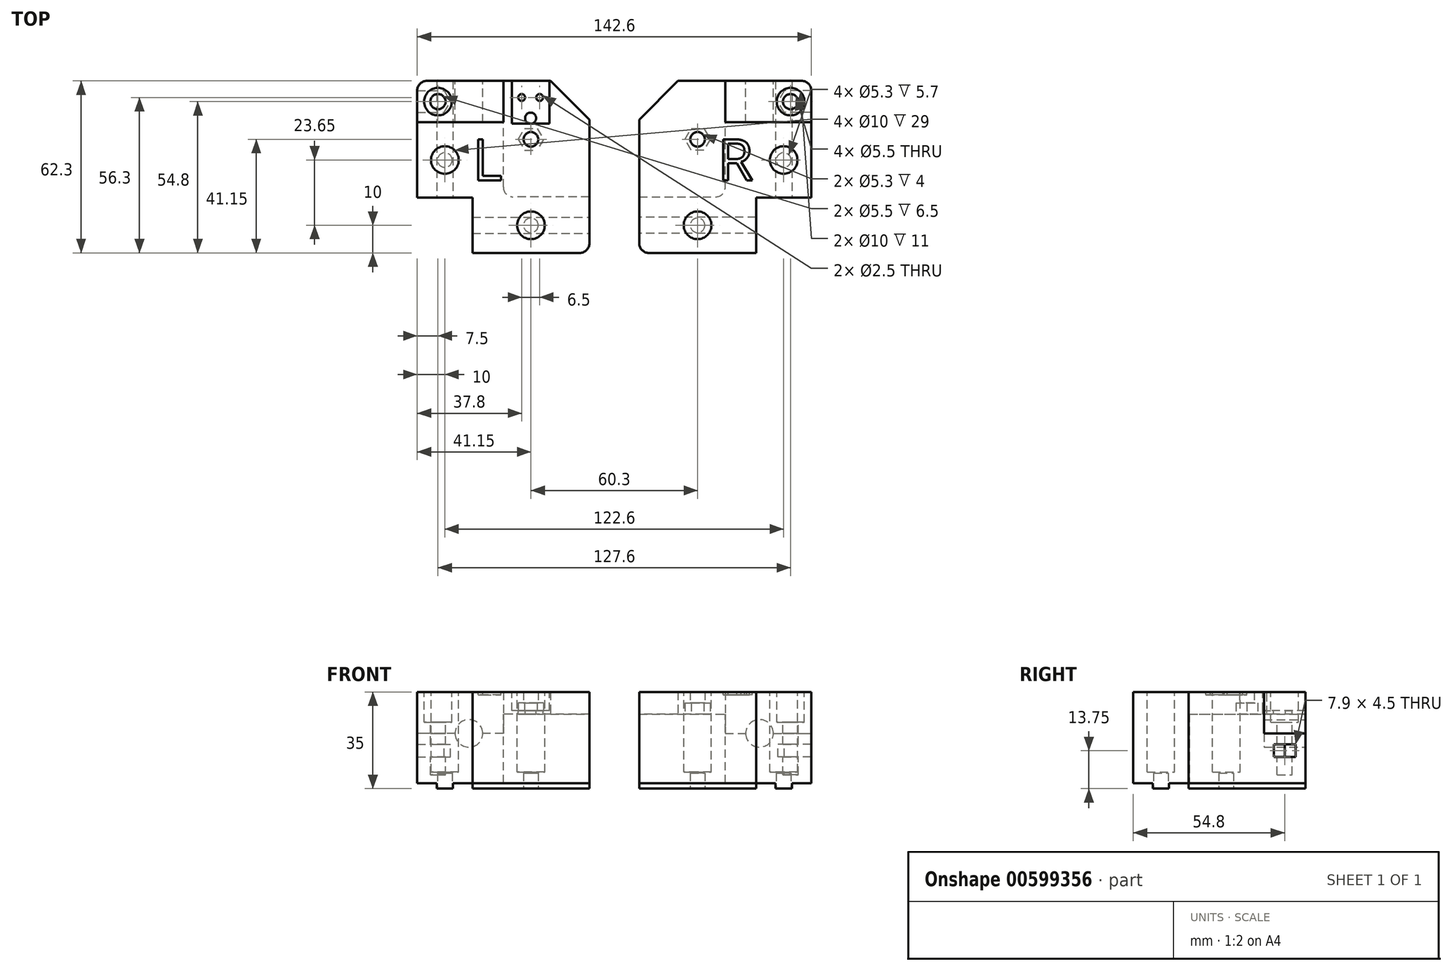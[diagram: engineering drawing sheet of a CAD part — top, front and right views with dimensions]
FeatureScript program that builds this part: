
annotation { "Feature Type Name" : "Feature", "Feature Type Description" : "" }
export const myFeature = defineFeature(function(context is Context, id is Id, definition is map)
    precondition{}
    {
        {
            var Q0;
            Q0=qCreatedBy(makeId("Top.planeOp"),FACE);
            var sketch = newSketch(context, id + "F0", { "sketchPlane" : qUnion([Q0])});
            skLineSegment(sketch, "E0.bottom", {"start": v(-21.15, 35) * mm, "end": v(41.15, 35) * mm});
            skLineSegment(sketch, "E0.top", {"start": v(-21.15, -27.3) * mm, "end": v(21.15, -27.3) * mm});
            skLineSegment(sketch, "E0.left", {"start": v(-21.15, 35) * mm, "end": v(-21.15, -27.3) * mm});
            skLineSegment(sketch, "E0.right", {"start": v(41.15, 35) * mm, "end": v(41.15, -7.3) * mm});
            skLineSegment(sketch, "E1.top", {"start": v(41.15, -7.3) * mm, "end": v(21.15, -7.3) * mm});
            skLineSegment(sketch, "E1.right", {"start": v(21.15, -27.3) * mm, "end": v(21.15, -7.3) * mm});
            skCircle(sketch, "E2", {"center": v(31.15, 13.85) * mm, "radius": 2.65 * mm});
            skPoint(sketch, "E3.centerSnap0", {"position": v(0, -27.3) * mm});
            skCircle(sketch, "E4", {"center": v(0, 13.85) * mm, "radius": 2.65 * mm});
            skPoint(sketch, "E5.centerSnap0", {"position": v(21.15, -17.3) * mm});
            skCircle(sketch, "E6", {"center": v(7.5, -17.3) * mm, "radius": 2.65 * mm});
            skSolve(sketch);
        }
        {
            var Q0;
            Q0=qSketchRegion(id+"F0",true);
            extrude(context, id + "F1", {"entities" : qUnion([Q0]), "depth" : 33 * mm});
        }
        {
            var Q0;
            Q0=makeQuery(id+"F1.opExtrude","CAP_FACE",FACE,{"disambiguationData":[OSD([sQuery(id+"F0.wireOp",EDGE,"E0.bottom"),sQuery(id+"F0.wireOp",EDGE,"E0.top"),sQuery(id+"F0.wireOp",EDGE,"E0.left"),sQuery(id+"F0.wireOp",EDGE,"E0.right"),sQuery(id+"F0.wireOp",EDGE,"E1.top"),sQuery(id+"F0.wireOp",EDGE,"E1.right"),sQuery(id+"F0.wireOp",EDGE,"E2"),sQuery(id+"F0.wireOp",EDGE,"74evYqRE-stiJ-cLZB-LkAt-MwOgdlZv3zJH"),sQuery(id+"F0.wireOp",EDGE,"YSbFCtBf-OZUa-blBg-jqSk-ddDIdjAn90QF"),sQuery(id+"F0.wireOp",EDGE,"E3"),sQuery(id+"F0.wireOp",EDGE,"E4")])],"isStart":true});
            var sketch = newSketch(context, id + "F2", { "sketchPlane" : qUnion([Q0])});
            skCircle(sketch, "E7.0", {"center": v(0, -13.85) * mm, "radius": 2.65 * mm, "construction": true});
            skCircle(sketch, "E8", {"center": v(0, -13.85) * mm, "radius": 3.95 * mm, "construction": true});
            skLineSegment(sketch, "E9", {"start": v(0, -20.58) * mm, "end": v(0, -4.16) * mm, "construction": true});
            skLineSegment(sketch, "E10", {"start": v(-6.74, -13.85) * mm, "end": v(6.1, -13.85) * mm, "construction": true});
            skLineSegment(sketch, "E11", {"start": v(-3.95, -16.13) * mm, "end": v(-3.95, -11.57) * mm});
            skLineSegment(sketch, "E12", {"start": v(-3.95, -11.57) * mm, "end": v(0, -9.29) * mm});
            skLineSegment(sketch, "E13", {"start": v(3.95, -16.13) * mm, "end": v(0, -18.41) * mm});
            skLineSegment(sketch, "E14", {"start": v(0, -18.41) * mm, "end": v(-3.95, -16.13) * mm});
            skLineSegment(sketch, "E15", {"start": v(3.95, -16.13) * mm, "end": v(3.95, -11.57) * mm});
            skLineSegment(sketch, "E16", {"start": v(3.95, -11.57) * mm, "end": v(0, -9.29) * mm});
            skSolve(sketch);
        }
        {
            var Q0;
            Q0=qSketchRegion(id+"F2",true);
            extrude(context, id + "F3", {"entities" : qUnion([Q0]), "operationType" : NewBodyOperationType.REMOVE, "oppositeDirection" : true, "depth" : 29 * mm});
        }
        {
            var Q0;
            Q0=makeQuery(id+"F1.opExtrude","CAP_FACE",FACE,{"disambiguationData":[OSD([sQuery(id+"F0.wireOp",EDGE,"E0.bottom"),sQuery(id+"F0.wireOp",EDGE,"E0.top"),sQuery(id+"F0.wireOp",EDGE,"E0.left"),sQuery(id+"F0.wireOp",EDGE,"E0.right"),sQuery(id+"F0.wireOp",EDGE,"E1.top"),sQuery(id+"F0.wireOp",EDGE,"E1.right"),sQuery(id+"F0.wireOp",EDGE,"E2"),sQuery(id+"F0.wireOp",EDGE,"74evYqRE-stiJ-cLZB-LkAt-MwOgdlZv3zJH"),sQuery(id+"F0.wireOp",EDGE,"YSbFCtBf-OZUa-blBg-jqSk-ddDIdjAn90QF"),sQuery(id+"F0.wireOp",EDGE,"E3"),sQuery(id+"F0.wireOp",EDGE,"E4")])],"isStart":false});
            var sketch = newSketch(context, id + "F4", { "sketchPlane" : qUnion([Q0])});
            skCircle(sketch, "E17.0", {"center": v(31.15, 13.85) * mm, "radius": 2.65 * mm, "construction": true});
            skCircle(sketch, "E18", {"center": v(31.15, 13.85) * mm, "radius": 5 * mm});
            skPoint(sketch, "E19", {"position": v(7.5, -17.3) * mm});
            skCircle(sketch, "E20", {"center": v(7.5, -17.3) * mm, "radius": 5 * mm});
            skSolve(sketch);
        }
        {
            var Q0;
            Q0=qSketchRegion(id+"F4",true);
            extrude(context, id + "F5", {"entities" : qUnion([Q0]), "operationType" : NewBodyOperationType.REMOVE, "oppositeDirection" : true, "depth" : 29 * mm});
        }
        {
            var Q0;
            Q0=makeQuery(id+"F1.opExtrude","CAP_FACE",FACE,{"disambiguationData":[OSD([sQuery(id+"F0.wireOp",EDGE,"E0.bottom"),sQuery(id+"F0.wireOp",EDGE,"E0.top"),sQuery(id+"F0.wireOp",EDGE,"E0.left"),sQuery(id+"F0.wireOp",EDGE,"E0.right"),sQuery(id+"F0.wireOp",EDGE,"E1.top"),sQuery(id+"F0.wireOp",EDGE,"E1.right"),sQuery(id+"F0.wireOp",EDGE,"E2"),sQuery(id+"F0.wireOp",EDGE,"74evYqRE-stiJ-cLZB-LkAt-MwOgdlZv3zJH"),sQuery(id+"F0.wireOp",EDGE,"YSbFCtBf-OZUa-blBg-jqSk-ddDIdjAn90QF"),sQuery(id+"F0.wireOp",EDGE,"E3"),sQuery(id+"F0.wireOp",EDGE,"E4")])],"isStart":true});
            var sketch = newSketch(context, id + "F6", { "sketchPlane" : qUnion([Q0])});
            skLineSegment(sketch, "E21.bottom", {"start": v(28.2, 7.3) * mm, "end": v(34.1, 7.3) * mm});
            skLineSegment(sketch, "E21.top", {"start": v(28.2, -35) * mm, "end": v(34.1, -35) * mm});
            skLineSegment(sketch, "E21.left", {"start": v(28.2, 7.3) * mm, "end": v(28.2, -13.57) * mm});
            skLineSegment(sketch, "E21.right", {"start": v(34.1, 7.3) * mm, "end": v(34.1, -13.57) * mm});
            skCircle(sketch, "E22.0", {"center": v(31.15, -13.85) * mm, "radius": 2.65 * mm});
            skLineSegment(sketch, "E23.trimOffspring", {"start": v(28.2, -13.57) * mm, "end": v(28.2, -35) * mm});
            skLineSegment(sketch, "E24.trimOffspring", {"start": v(34.1, -13.57) * mm, "end": v(34.1, -35) * mm});
            skLineSegment(sketch, "E25.bottom", {"start": v(-21.15, 20.25) * mm, "end": v(21.15, 20.25) * mm});
            skLineSegment(sketch, "E25.top", {"start": v(-21.15, 14.35) * mm, "end": v(21.15, 14.35) * mm});
            skLineSegment(sketch, "E25.left", {"start": v(-21.15, 20.25) * mm, "end": v(-21.15, 14.35) * mm});
            skLineSegment(sketch, "E25.right", {"start": v(21.15, 20.25) * mm, "end": v(21.15, 14.35) * mm});
            skCircle(sketch, "E26.0", {"center": v(7.5, 17.3) * mm, "radius": 2.65 * mm});
            skSolve(sketch);
        }
        {
            var Q0;
            Q0=qSketchRegion(id+"F6",true);
            extrude(context, id + "F7", {"entities" : qUnion([Q0]), "operationType" : NewBodyOperationType.ADD, "depth" : 2 * mm});
        }
        {
            var Q0;
            Q0=makeQuery(id+"F1.opExtrude","SWEPT_EDGE",EDGE,{"disambiguationData":[OSD([sQuery(id+"F0.wireOp",EDGE,"E0.bottom"),sQuery(id+"F0.wireOp",EDGE,"E0.right")])]});
            fillet(context, id + "F8", {"entities" : qUnion([Q0]), "radius" : 3.5 * mm, "tangentPropagation" : true, "allowEdgeOverflow" : false});
        }
        {
            var Q0;
            Q0=makeQuery(id+"F7.boolean.opBoolean","MERGE",FACE,{"derivedFrom":[makeQuery(id+"F1.opExtrude","SWEPT_FACE",FACE,{"disambiguationData":[OSD([sQuery(id+"F0.wireOp",EDGE,"E0.left")])]}),makeQuery(id+"F7.opExtrude","SWEPT_FACE",FACE,{"disambiguationData":[OSD([sQuery(id+"F6.wireOp",EDGE,"E25.left")])]})]});
            var sketch = newSketch(context, id + "F9", { "sketchPlane" : qUnion([Q0])});
            skPoint(sketch, "E27.oppositeSnap0", {"position": v(-3.85, 33) * mm});
            skLineSegment(sketch, "E27.bottom", {"start": v(-3.85, 0) * mm, "end": v(-35, 0) * mm});
            skLineSegment(sketch, "E27.top", {"start": v(-35, 25) * mm, "end": v(-3.85, 25) * mm});
            skLineSegment(sketch, "E27.left", {"start": v(-35, 0) * mm, "end": v(-35, 25) * mm});
            skLineSegment(sketch, "E27.right", {"start": v(-3.85, 0) * mm, "end": v(-3.85, 25) * mm});
            skSolve(sketch);
        }
        {
            var Q0;
            Q0=qSketchRegion(id+"F9",true);
            extrude(context, id + "F10", {"entities" : qUnion([Q0]), "operationType" : NewBodyOperationType.REMOVE, "oppositeDirection" : true, "depth" : 42 * mm});
        }
        {
            var Q0;
            Q0=makeQuery(id+"F10.boolean.opBoolean","COPY",EDGE,{"derivedFrom":makeQuery(id+"F10.opExtrude","CAP_EDGE",EDGE,{"disambiguationData":[OSD([sQuery(id+"F9.wireOp",EDGE,"E27.right")])],"isStart":false})});
            var Q1;
            Q1=makeQuery(id+"F10.boolean.opBoolean","COPY",EDGE,{"derivedFrom":makeQuery(id+"F10.opExtrude","CAP_EDGE",EDGE,{"disambiguationData":[OSD([sQuery(id+"F9.wireOp",EDGE,"E27.left")])],"isStart":false})});
            fillet(context, id + "F11", {"entities" : qUnion([Q0, Q1]), "radius" : 3.5 * mm, "tangentPropagation" : true, "allowEdgeOverflow" : false});
        }
        {
            var Q0;
            Q0=makeQuery(id+"F5.boolean.opBoolean","COPY",FACE,{"derivedFrom":makeQuery(id+"F5.opExtrude","CAP_FACE",FACE,{"disambiguationData":[OSD([sQuery(id+"F4.wireOp",EDGE,"E20")])],"isStart":false})});
            var sketch = newSketch(context, id + "F12", { "sketchPlane" : qUnion([Q0])});
            skCircle(sketch, "E28.0", {"center": v(31.15, 13.85) * mm, "radius": 2.65 * mm});
            skCircle(sketch, "E29.0", {"center": v(7.5, -17.3) * mm, "radius": 2.65 * mm});
            skSolve(sketch);
        }
        {
            var Q0;
            Q0=qSketchRegion(id+"F12",true);
            extrude(context, id + "F13", {"entities" : qUnion([Q0]), "operationType" : NewBodyOperationType.ADD, "oppositeDirection" : true, "depth" : 0.3 * mm});
        }
        {
            var Q0;
            Q0=makeQuery(id+"F1.opExtrude","CAP_FACE",FACE,{"disambiguationData":[OSD([sQuery(id+"F0.wireOp",EDGE,"E0.bottom"),sQuery(id+"F0.wireOp",EDGE,"E0.top"),sQuery(id+"F0.wireOp",EDGE,"E0.left"),sQuery(id+"F0.wireOp",EDGE,"E0.right"),sQuery(id+"F0.wireOp",EDGE,"E1.top"),sQuery(id+"F0.wireOp",EDGE,"E1.right"),sQuery(id+"F0.wireOp",EDGE,"E2"),sQuery(id+"F0.wireOp",EDGE,"E4"),sQuery(id+"F0.wireOp",EDGE,"E6")])],"isStart":false});
            cPlane(context, id + "F14", {"entities" : qUnion([Q0]), "cplaneType" : CPlaneType.OFFSET, "offset" : 15 * mm, "oppositeDirection" : true, "width" : 150 * mm, "height" : 150 * mm});
        }
        {
            var Q0;
            Q0=qCreatedBy(id+"F14.planeOp",FACE);
            var sketch = newSketch(context, id + "F15", { "sketchPlane" : qUnion([Q0])});
            skLineSegment(sketch, "E30.0", {"start": v(-21.15, 3.85) * mm, "end": v(-21.15, -27.3) * mm});
            skLineSegment(sketch, "E31.0", {"start": v(-21.15, -27.3) * mm, "end": v(-6.15, -27.3) * mm});
            skPoint(sketch, "E32.0", {"position": v(-21.15, 3.85) * mm});
            skLineSegment(sketch, "E33", {"start": v(-21.15, 3.85) * mm, "end": v(-6.15, 3.85) * mm});
            skLineSegment(sketch, "E34", {"start": v(-6.15, 3.85) * mm, "end": v(-6.15, -27.3) * mm});
            skPoint(sketch, "E35.orphan", {"position": v(21.15, -27.3) * mm});
            skSolve(sketch);
        }
        {
            var Q0;
            Q0=qSketchRegion(id+"F15",true);
            extrude(context, id + "F16", {"entities" : qUnion([Q0]), "operationType" : NewBodyOperationType.REMOVE, "depth" : 15 * mm});
        }
        {
            var Q0;
            Q0=makeQuery(id+"F16.boolean.opBoolean","COPY",FACE,{"derivedFrom":makeQuery(id+"F16.opExtrude","CAP_FACE",FACE,{"disambiguationData":[OSD([sQuery(id+"F15.wireOp",EDGE,"E30.0"),sQuery(id+"F15.wireOp",EDGE,"E31.0"),sQuery(id+"F15.wireOp",EDGE,"E33"),sQuery(id+"F15.wireOp",EDGE,"E34")])],"isStart":true})});
            var sketch = newSketch(context, id + "F17", { "sketchPlane" : qUnion([Q0])});
            skLineSegment(sketch, "E36.0.0", {"start": v(-6.15, -27.3) * mm, "end": v(-6.15, 3.85) * mm});
            skLineSegment(sketch, "E36.0.1", {"start": v(-6.15, 3.85) * mm, "end": v(-21.15, 3.85) * mm});
            skLineSegment(sketch, "E36.0.2", {"start": v(-21.15, 3.85) * mm, "end": v(-21.15, -27.3) * mm});
            skLineSegment(sketch, "E36.0.3", {"start": v(-21.15, -27.3) * mm, "end": v(-6.15, -27.3) * mm});
            skSolve(sketch);
        }
        {
            var Q0;
            Q0=qSketchRegion(id+"F17",true);
            extrude(context, id + "F18", {"entities" : qUnion([Q0]), "depth" : 15 * mm});
        }
        {
            var Q0;
            Q0=makeQuery(id+"F1.opExtrude","SWEPT_FACE",FACE,{"disambiguationData":[OSD([sQuery(id+"F0.wireOp",EDGE,"E0.left")])]});
            var sketch = newSketch(context, id + "F19", { "sketchPlane" : qUnion([Q0])});
            skCircle(sketch, "E37", {"center": v(8.58, 18) * mm, "radius": 5 * mm});
            skSolve(sketch);
        }
        {
            var Q0;
            Q0=qSketchRegion(id+"F19",true);
            extrude(context, id + "F20", {"entities" : qUnion([Q0]), "operationType" : NewBodyOperationType.REMOVE, "oppositeDirection" : true, "depth" : 15 * mm});
        }
        {
            var Q0;
            Q0=makeQuery(id+"F18.opExtrude","CAP_FACE",FACE,{"disambiguationData":[OSD([sQuery(id+"F17.wireOp",EDGE,"E36.0.0"),sQuery(id+"F17.wireOp",EDGE,"E36.0.1"),sQuery(id+"F17.wireOp",EDGE,"E36.0.2"),sQuery(id+"F17.wireOp",EDGE,"E36.0.3")])],"isStart":false});
            var sketch = newSketch(context, id + "F21", { "sketchPlane" : qUnion([Q0])});
            skCircle(sketch, "E38", {"center": v(-13.65, -19.8) * mm, "radius": 2.75 * mm});
            skSolve(sketch);
        }
        {
            var Q0;
            Q0=qSketchRegion(id+"F21",true);
            extrude(context, id + "F22", {"entities" : qUnion([Q0]), "operationType" : NewBodyOperationType.REMOVE, "oppositeDirection" : true, "depth" : 30 * mm});
        }
        {
            var Q0;
            Q0=makeQuery(id+"F18.opExtrude","CAP_FACE",FACE,{"disambiguationData":[OSD([sQuery(id+"F17.wireOp",EDGE,"E36.0.0"),sQuery(id+"F17.wireOp",EDGE,"E36.0.1"),sQuery(id+"F17.wireOp",EDGE,"E36.0.2"),sQuery(id+"F17.wireOp",EDGE,"E36.0.3")])],"isStart":false});
            var sketch = newSketch(context, id + "F23", { "sketchPlane" : qUnion([Q0])});
            skPoint(sketch, "E39", {"position": v(-13.65, -19.8) * mm});
            skCircle(sketch, "E40", {"center": v(-13.65, -19.8) * mm, "radius": 5 * mm});
            skSolve(sketch);
        }
        {
            var Q0;
            Q0=qSketchRegion(id+"F23",true);
            extrude(context, id + "F24", {"entities" : qUnion([Q0]), "operationType" : NewBodyOperationType.REMOVE, "oppositeDirection" : true, "depth" : 11 * mm});
        }
        {
            var Q0;
            Q0=qCreatedBy(id+"F14.planeOp",FACE);
            cPlane(context, id + "F25", {"entities" : qUnion([Q0]), "cplaneType" : CPlaneType.OFFSET, "offset" : 4 * mm, "oppositeDirection" : true, "width" : 150 * mm, "height" : 150 * mm});
        }
        {
            var Q0;
            Q0=qCreatedBy(id+"F25.planeOp",FACE);
            var sketch = newSketch(context, id + "F26", { "sketchPlane" : qUnion([Q0])});
            skCircle(sketch, "E41.0", {"center": v(-13.65, -19.8) * mm, "radius": 2.75 * mm, "construction": true});
            skCircle(sketch, "E42.0", {"center": v(-13.65, -19.8) * mm, "radius": 2.65 * mm, "construction": true});
            skCircle(sketch, "E43", {"center": v(-13.65, -19.8) * mm, "radius": 3.95 * mm, "construction": true});
            skLineSegment(sketch, "E44", {"start": v(-20.39, -19.8) * mm, "end": v(-7.56, -19.8) * mm, "construction": true});
            skLineSegment(sketch, "E45", {"start": v(-17.6, -22.08) * mm, "end": v(-17.6, -17.52) * mm});
            skLineSegment(sketch, "E46", {"start": v(-17.6, -17.52) * mm, "end": v(-13.65, -15.24) * mm});
            skLineSegment(sketch, "E47", {"start": v(-9.7, -22.08) * mm, "end": v(-13.65, -24.36) * mm});
            skLineSegment(sketch, "E48", {"start": v(-13.65, -24.36) * mm, "end": v(-17.6, -22.08) * mm});
            skLineSegment(sketch, "E49", {"start": v(-9.7, -22.08) * mm, "end": v(-9.7, -17.52) * mm});
            skLineSegment(sketch, "E50", {"start": v(-9.7, -17.52) * mm, "end": v(-13.65, -15.24) * mm});
            skLineSegment(sketch, "E51", {"start": v(-17.6, -22.08) * mm, "end": v(-17.6, -27.3) * mm});
            skLineSegment(sketch, "E52", {"start": v(-17.6, -27.3) * mm, "end": v(-9.7, -27.3) * mm});
            skLineSegment(sketch, "E53", {"start": v(-9.7, -27.3) * mm, "end": v(-9.7, -22.08) * mm});
            skSolve(sketch);
        }
        {
            var Q0;
            Q0=qSketchRegion(id+"F26",true);
            extrude(context, id + "F27", {"entities" : qUnion([Q0]), "operationType" : NewBodyOperationType.REMOVE, "oppositeDirection" : true, "depth" : 4.5 * mm});
        }
        {
            var Q0;
            Q0=makeQuery(id+"F1.opExtrude","SWEPT_EDGE",EDGE,{"disambiguationData":[OSD([sQuery(id+"F0.wireOp",EDGE,"E0.top"),sQuery(id+"F0.wireOp",EDGE,"E0.left")])]});
            var Q1;
            Q1=makeQuery(id+"F18.opExtrude","SWEPT_EDGE",EDGE,{"disambiguationData":[OSD([sQuery(id+"F17.wireOp",EDGE,"E36.0.2"),sQuery(id+"F17.wireOp",EDGE,"E36.0.3")])]});
            fillet(context, id + "F28", {"entities" : qUnion([Q0, Q1]), "radius" : 3.5 * mm, "tangentPropagation" : true, "allowEdgeOverflow" : false});
        }
        {
            var Q0;
            Q0=makeQuery(id+"F1.opExtrude","SWEPT_EDGE",EDGE,{"disambiguationData":[OSD([sQuery(id+"F0.wireOp",EDGE,"E0.bottom"),sQuery(id+"F0.wireOp",EDGE,"E0.left")])]});
            chamfer(context, id + "F29", {"entities" : qUnion([Q0]), "width" : 14 * mm, "tangentPropagation" : true});
        }
        {
            var Q0;
            Q0=makeQuery(id+"F1.opExtrude","SWEPT_BODY",BODY,{"disambiguationData":[OSD([sQuery(id+"F0.wireOp",EDGE,"E0.bottom"),sQuery(id+"F0.wireOp",EDGE,"E0.top"),sQuery(id+"F0.wireOp",EDGE,"E0.left"),sQuery(id+"F0.wireOp",EDGE,"E0.right"),sQuery(id+"F0.wireOp",EDGE,"E1.top"),sQuery(id+"F0.wireOp",EDGE,"E1.right"),sQuery(id+"F0.wireOp",EDGE,"E2"),sQuery(id+"F0.wireOp",EDGE,"74evYqRE-stiJ-cLZB-LkAt-MwOgdlZv3zJH"),sQuery(id+"F0.wireOp",EDGE,"YSbFCtBf-OZUa-blBg-jqSk-ddDIdjAn90QF"),sQuery(id+"F0.wireOp",EDGE,"E3"),sQuery(id+"F0.wireOp",EDGE,"E4")])]});
            var Q1;
            Q1=makeQuery(id+"F18.opExtrude","SWEPT_BODY",BODY,{"disambiguationData":[OSD([sQuery(id+"F17.wireOp",EDGE,"E36.0.0"),sQuery(id+"F17.wireOp",EDGE,"E36.0.1"),sQuery(id+"F17.wireOp",EDGE,"E36.0.2"),sQuery(id+"F17.wireOp",EDGE,"E36.0.3")])]});
            var Q2;
            Q2=makeQuery(id+"F1.opExtrude","SWEPT_FACE",FACE,{"disambiguationData":[OSD([sQuery(id+"F0.wireOp",EDGE,"E0.right")])]});
            mirror(context, id + "F30", {"entities" : qUnion([Q0, Q1]), "mirrorPlane" : qUnion([Q2])});
        }
        {
            var Q0;
            Q0=makeQuery(id+"F1.opExtrude","CAP_FACE",FACE,{"disambiguationData":[OSD([sQuery(id+"F0.wireOp",EDGE,"E0.bottom"),sQuery(id+"F0.wireOp",EDGE,"E0.top"),sQuery(id+"F0.wireOp",EDGE,"E0.left"),sQuery(id+"F0.wireOp",EDGE,"E0.right"),sQuery(id+"F0.wireOp",EDGE,"E1.top"),sQuery(id+"F0.wireOp",EDGE,"E1.right"),sQuery(id+"F0.wireOp",EDGE,"E2"),sQuery(id+"F0.wireOp",EDGE,"74evYqRE-stiJ-cLZB-LkAt-MwOgdlZv3zJH"),sQuery(id+"F0.wireOp",EDGE,"E3"),sQuery(id+"F0.wireOp",EDGE,"E4")])],"isStart":false});
            var sketch = newSketch(context, id + "F31", { "sketchPlane" : qUnion([Q0])});
            skLineSegment(sketch, "E54.bottom", {"start": v(-21.15, 20.6) * mm, "end": v(-13.65, 20.6) * mm});
            skLineSegment(sketch, "E54.top", {"start": v(-21.15, 6.9) * mm, "end": v(-13.65, 6.9) * mm});
            skLineSegment(sketch, "E54.left", {"start": v(-21.15, 20.6) * mm, "end": v(-21.15, 6.9) * mm});
            skLineSegment(sketch, "E54.right", {"start": v(-13.65, 20.6) * mm, "end": v(-13.65, 6.9) * mm});
            skLineSegment(sketch, "E55.bottom", {"start": v(-13.65, 20.6) * mm, "end": v(-5.65, 20.6) * mm});
            skLineSegment(sketch, "E55.top", {"start": v(-13.65, 6.9) * mm, "end": v(-5.65, 6.9) * mm});
            skLineSegment(sketch, "E55.left", {"start": v(-13.65, 20.6) * mm, "end": v(-13.65, 6.9) * mm, "construction": true});
            skLineSegment(sketch, "E55.right", {"start": v(-5.65, 20.6) * mm, "end": v(-5.65, 6.9) * mm});
            skSolve(sketch);
        }
        {
            var Q0;
            Q0=qSketchRegion(id+"F31",true);
            extrude(context, id + "F32", {"entities" : qUnion([Q0]), "operationType" : NewBodyOperationType.REMOVE, "oppositeDirection" : true, "depth" : 6.8 * mm});
        }
        {
            var Q0;
            Q0=makeQuery(id+"F32.boolean.opBoolean","COPY",FACE,{"derivedFrom":makeQuery(id+"F32.opExtrude","CAP_FACE",FACE,{"disambiguationData":[OSD([sQuery(id+"F31.wireOp",EDGE,"E54.bottom"),sQuery(id+"F31.wireOp",EDGE,"E54.top"),sQuery(id+"F31.wireOp",EDGE,"E54.left"),sQuery(id+"F31.wireOp",EDGE,"E54.right")])],"isStart":false})});
            var sketch = newSketch(context, id + "F33", { "sketchPlane" : qUnion([Q0])});
            skCircle(sketch, "E56", {"center": v(-15.15, 17) * mm, "radius": 1.25 * mm});
            skCircle(sketch, "E57", {"center": v(-15.15, 10.5) * mm, "radius": 1.25 * mm});
            skSolve(sketch);
        }
        {
            var Q0;
            Q0=qSketchRegion(id+"F33",true);
            extrude(context, id + "F34", {"entities" : qUnion([Q0]), "operationType" : NewBodyOperationType.REMOVE, "oppositeDirection" : true, "depth" : 8 * mm});
        }
        {
            var Q0;
            Q0=makeQuery(id+"F32.boolean.opBoolean","COPY",FACE,{"derivedFrom":makeQuery(id+"F32.opExtrude","CAP_FACE",FACE,{"disambiguationData":[OSD([sQuery(id+"F31.wireOp",EDGE,"E54.bottom"),sQuery(id+"F31.wireOp",EDGE,"E54.top"),sQuery(id+"F31.wireOp",EDGE,"E54.left"),sQuery(id+"F31.wireOp",EDGE,"E55.bottom"),sQuery(id+"F31.wireOp",EDGE,"E55.top"),sQuery(id+"F31.wireOp",EDGE,"E55.right")])],"isStart":false})});
            var sketch = newSketch(context, id + "F35", { "sketchPlane" : qUnion([Q0])});
            skCircle(sketch, "E58", {"center": v(-7.65, 13.75) * mm, "radius": 2 * mm});
            skPoint(sketch, "E58.centerSnap0", {"position": v(-5.65, 13.75) * mm});
            skSolve(sketch);
        }
        {
            var Q0;
            Q0=qSketchRegion(id+"F35",true);
            extrude(context, id + "F36", {"entities" : qUnion([Q0]), "operationType" : NewBodyOperationType.REMOVE, "oppositeDirection" : true, "depth" : 30 * mm});
        }
        {
            var Q0;
            Q0=makeQuery(id+"F18.opExtrude","SWEPT_BODY",BODY,{"disambiguationData":[OSD([sQuery(id+"F17.wireOp",EDGE,"E36.0.0"),sQuery(id+"F17.wireOp",EDGE,"E36.0.1"),sQuery(id+"F17.wireOp",EDGE,"E36.0.2"),sQuery(id+"F17.wireOp",EDGE,"E36.0.3")])]});
            var Q1;
            Q1=makeQuery(id+"F1.opExtrude","SWEPT_BODY",BODY,{"disambiguationData":[OSD([sQuery(id+"F0.wireOp",EDGE,"E0.bottom"),sQuery(id+"F0.wireOp",EDGE,"E0.top"),sQuery(id+"F0.wireOp",EDGE,"E0.left"),sQuery(id+"F0.wireOp",EDGE,"E0.right"),sQuery(id+"F0.wireOp",EDGE,"E1.top"),sQuery(id+"F0.wireOp",EDGE,"E1.right"),sQuery(id+"F0.wireOp",EDGE,"E2"),sQuery(id+"F0.wireOp",EDGE,"E4"),sQuery(id+"F0.wireOp",EDGE,"E6")])]});
            var Q2;
            {var subQ0=sQuery(id+"F0.wireOp",EDGE,"E0.top");Q2=makeQuery(id+"F28.opFillet","BLEND_EDGE",EDGE,{"blendedFrom":[makeQuery(id+"F1.opExtrude","SWEPT_EDGE",EDGE,{"disambiguationData":[OSD([subQ0,sQuery(id+"F0.wireOp",EDGE,"E0.left")])]}),makeQuery(id+"F1.opExtrude","SWEPT_FACE",FACE,{"disambiguationData":[OSD([subQ0])]})],"blendedInto":[makeQuery(id+"F1.opExtrude","SWEPT_FACE",FACE,{"disambiguationData":[OSD([subQ0])]})]});}
            transform(context, id + "F37", {"entities" : qUnion([Q0, Q1]), "transformType" : TransformType.ROTATION, "transformAxis" : qUnion([Q2]), "angle" : 90 * degree, "makeCopy" : false});
        }
        {
            var Q0;
            Q0=makeQuery(id+"F30.opPattern","COPY",BODY,{"derivedFrom":makeQuery(id+"F1.opExtrude","SWEPT_BODY",BODY,{"disambiguationData":[OSD([sQuery(id+"F0.wireOp",EDGE,"E0.bottom"),sQuery(id+"F0.wireOp",EDGE,"E0.top"),sQuery(id+"F0.wireOp",EDGE,"E0.left"),sQuery(id+"F0.wireOp",EDGE,"E0.right"),sQuery(id+"F0.wireOp",EDGE,"E1.top"),sQuery(id+"F0.wireOp",EDGE,"E1.right"),sQuery(id+"F0.wireOp",EDGE,"E2"),sQuery(id+"F0.wireOp",EDGE,"E4"),sQuery(id+"F0.wireOp",EDGE,"E6")])]}),"instanceName":"1"});
            var Q1;
            Q1=makeQuery(id+"F30.opPattern","COPY",BODY,{"derivedFrom":makeQuery(id+"F18.opExtrude","SWEPT_BODY",BODY,{"disambiguationData":[OSD([sQuery(id+"F17.wireOp",EDGE,"E36.0.0"),sQuery(id+"F17.wireOp",EDGE,"E36.0.1"),sQuery(id+"F17.wireOp",EDGE,"E36.0.2"),sQuery(id+"F17.wireOp",EDGE,"E36.0.3")])]}),"instanceName":"1"});
            var Q2;
            {var subQ0=sQuery(id+"F0.wireOp",EDGE,"E0.top");Q2=makeQuery(id+"F30.opPattern","COPY",EDGE,{"derivedFrom":makeQuery(id+"F28.opFillet","BLEND_EDGE",EDGE,{"blendedFrom":[makeQuery(id+"F1.opExtrude","SWEPT_EDGE",EDGE,{"disambiguationData":[OSD([subQ0,sQuery(id+"F0.wireOp",EDGE,"E0.left")])]}),makeQuery(id+"F1.opExtrude","SWEPT_FACE",FACE,{"disambiguationData":[OSD([subQ0])]})],"blendedInto":[makeQuery(id+"F1.opExtrude","SWEPT_FACE",FACE,{"disambiguationData":[OSD([subQ0])]})]}),"instanceName":"1"});}
            transform(context, id + "F38", {"entities" : qUnion([Q0, Q1]), "transformType" : TransformType.ROTATION, "transformAxis" : qUnion([Q2]), "angle" : 270 * degree, "makeCopy" : false});
        }
        {
            var Q0;
            Q0=makeQuery(id+"F30.opPattern","COPY",BODY,{"derivedFrom":makeQuery(id+"F18.opExtrude","SWEPT_BODY",BODY,{"disambiguationData":[OSD([sQuery(id+"F17.wireOp",EDGE,"E36.0.0"),sQuery(id+"F17.wireOp",EDGE,"E36.0.1"),sQuery(id+"F17.wireOp",EDGE,"E36.0.2"),sQuery(id+"F17.wireOp",EDGE,"E36.0.3")])]}),"instanceName":"1"});
            var Q1;
            Q1=makeQuery(id+"F30.opPattern","COPY",BODY,{"derivedFrom":makeQuery(id+"F1.opExtrude","SWEPT_BODY",BODY,{"disambiguationData":[OSD([sQuery(id+"F0.wireOp",EDGE,"E0.bottom"),sQuery(id+"F0.wireOp",EDGE,"E0.top"),sQuery(id+"F0.wireOp",EDGE,"E0.left"),sQuery(id+"F0.wireOp",EDGE,"E0.right"),sQuery(id+"F0.wireOp",EDGE,"E1.top"),sQuery(id+"F0.wireOp",EDGE,"E1.right"),sQuery(id+"F0.wireOp",EDGE,"E2"),sQuery(id+"F0.wireOp",EDGE,"E4"),sQuery(id+"F0.wireOp",EDGE,"E6")])]}),"instanceName":"1"});
            var Q2;
            Q2=makeQuery(id+"F30.opPattern","COPY",EDGE,{"derivedFrom":makeQuery(id+"F1.opExtrude","SWEPT_EDGE",EDGE,{"disambiguationData":[OSD([sQuery(id+"F0.wireOp",EDGE,"E0.right"),sQuery(id+"F0.wireOp",EDGE,"E1.top")])]}),"instanceName":"1"});
            var Q3;
            Q3=makeQuery(id+"F30.opPattern","COPY",FACE,{"derivedFrom":makeQuery(id+"F7.boolean.opBoolean","MERGE",FACE,{"derivedFrom":[makeQuery(id+"F1.opExtrude","SWEPT_FACE",FACE,{"disambiguationData":[OSD([sQuery(id+"F0.wireOp",EDGE,"E1.top")])]}),makeQuery(id+"F7.opExtrude","SWEPT_FACE",FACE,{"disambiguationData":[OSD([sQuery(id+"F6.wireOp",EDGE,"E21.bottom")])]})]}),"instanceName":"1"});
            transform(context, id + "F39", {"entities" : qUnion([Q0, Q1]), "transformType" : TransformType.TRANSLATION_DISTANCE, "transformDirection" : qUnion([Q3]), "distance" : 25 * mm, "makeCopy" : false});
        }
        {
            var Q0;
            Q0=makeQuery(id+"F1.opExtrude","CAP_FACE",FACE,{"disambiguationData":[OSD([sQuery(id+"F0.wireOp",EDGE,"E0.bottom"),sQuery(id+"F0.wireOp",EDGE,"E0.top"),sQuery(id+"F0.wireOp",EDGE,"E0.left"),sQuery(id+"F0.wireOp",EDGE,"E0.right"),sQuery(id+"F0.wireOp",EDGE,"E1.top"),sQuery(id+"F0.wireOp",EDGE,"E1.right"),sQuery(id+"F0.wireOp",EDGE,"E2"),sQuery(id+"F0.wireOp",EDGE,"E4"),sQuery(id+"F0.wireOp",EDGE,"E6")])],"isStart":false});
            var sketch = newSketch(context, id + "F40", { "sketchPlane" : qUnion([Q0])});
            skText(sketch, "E59", { "text": "L", "fontName": "OpenSans-Regular.ttf"});
            skText(sketch, "E60", { "text": "R", "fontName": "OpenSans-Regular.ttf"});
            const initialGuessF40  = {"E59": [0.00235, -0.0598, 1, 0, 0.015], "E60": [0.09108, -0.0598, 1, 0, 0.015]};
            skSetInitialGuess(sketch, initialGuessF40);
            skSolve(sketch);
        }
        {
            var Q0;
            Q0=qSketchRegion(id+"F40",true);
            extrude(context, id + "F41", {"entities" : qUnion([Q0]), "operationType" : NewBodyOperationType.REMOVE, "oppositeDirection" : true, "depth" : 1 * mm});
        }
    });
